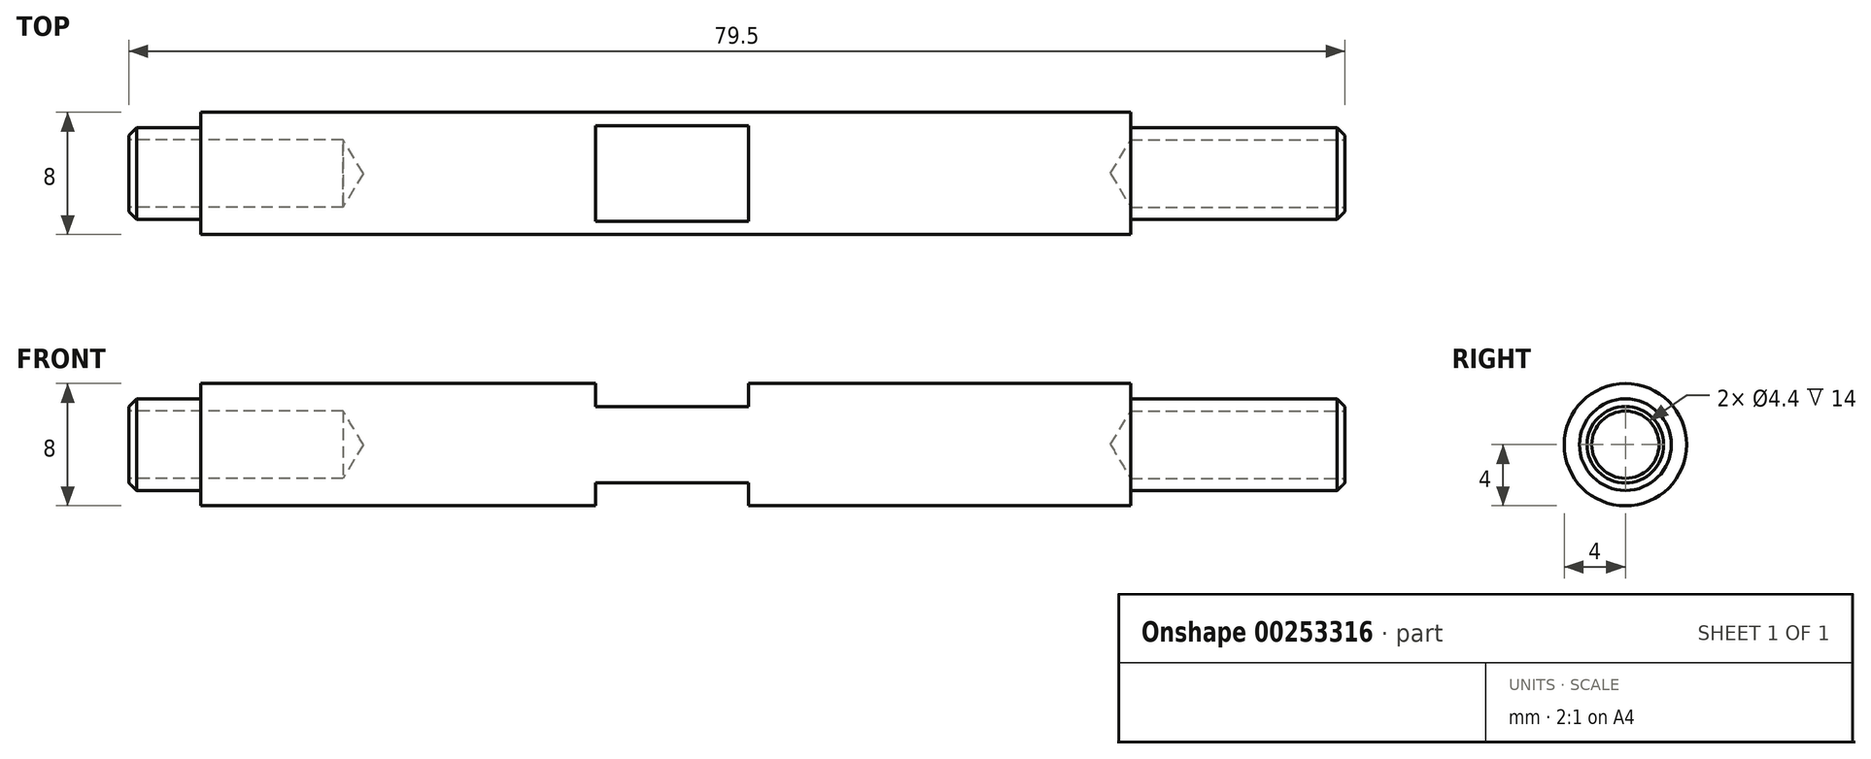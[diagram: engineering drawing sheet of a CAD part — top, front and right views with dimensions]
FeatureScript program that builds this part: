
annotation { "Feature Type Name" : "Feature", "Feature Type Description" : "" }
export const myFeature = defineFeature(function(context is Context, id is Id, definition is map)
    precondition{}
    {
        {
            var Q0;
            Q0=qCreatedBy(makeId("Top.planeOp"),FACE);
            var sketch = newSketch(context, id + "F0", { "sketchPlane" : qUnion([Q0])});
            skLineSegment(sketch, "E0.bottom", {"start": v(30.4, 4) * mm, "end": v(-30.4, 4) * mm});
            skLineSegment(sketch, "E0.top", {"start": v(30.4, -4) * mm, "end": v(-30.4, -4) * mm, "construction": true});
            skLineSegment(sketch, "E0.left", {"start": v(30.4, 4) * mm, "end": v(30.4, -4) * mm});
            skLineSegment(sketch, "E0.right", {"start": v(-30.4, 4) * mm, "end": v(-30.4, -4) * mm});
            skPoint(sketch, "E0.middle", {"position": v(0, 0) * mm});
            skLineSegment(sketch, "E1", {"start": v(30.4, 3) * mm, "end": v(44.4, 3) * mm});
            skLineSegment(sketch, "E2", {"start": v(44.4, 3) * mm, "end": v(44.4, -3) * mm});
            skLineSegment(sketch, "E3", {"start": v(44.4, -3) * mm, "end": v(30.4, -3) * mm, "construction": true});
            skLineSegment(sketch, "E4", {"start": v(-30.4, 3) * mm, "end": v(-35.1, 3) * mm});
            skLineSegment(sketch, "E5", {"start": v(-35.1, 3) * mm, "end": v(-35.1, -3) * mm});
            skLineSegment(sketch, "E6", {"start": v(-35.1, -3) * mm, "end": v(-30.4, -3) * mm, "construction": true});
            skLineSegment(sketch, "E7", {"start": v(-49.35, 0) * mm, "end": v(55.64, 0) * mm});
            skPoint(sketch, "E7.endSnap0", {"position": v(44.4, 0) * mm});
            skPoint(sketch, "E8", {"position": v(-35.1, 0) * mm});
            skSolve(sketch);
        }
        {
            var Q0;
            {var subQ0=sQuery(id+"F0.wireOp",EDGE,"E4");Q0=makeQuery(id+"F0.imprint","IMPRINT",FACE,{"disambiguationData":[TD([[makeQuery(id+"F0.imprint","IMPRINT",EDGE,{"derivedFrom":subQ0}),1.0]])]});}
            var Q1;
            {var subQ3=sQuery(id+"F0.wireOp",EDGE,"E0.bottom");Q1=makeQuery(id+"F0.imprint","IMPRINT",FACE,{"disambiguationData":[TD([[makeQuery(id+"F0.imprint","IMPRINT",EDGE,{"derivedFrom":subQ3}),1.0]])]});}
            var Q2;
            {var subQ0=sQuery(id+"F0.wireOp",EDGE,"E1");Q2=makeQuery(id+"F0.imprint","IMPRINT",FACE,{"disambiguationData":[TD([[makeQuery(id+"F0.imprint","IMPRINT",EDGE,{"derivedFrom":subQ0}),-1.0]])]});}
            var Q3;
            Q3=sQuery(id+"F0.wireOp",EDGE,"E7");
            revolve(context, id + "F1", {"entities" : qUnion([Q0, Q1, Q2]), "axis" : qUnion([Q3]), "revolveType" : RevolveType.FULL});
        }
        {
            var Q0;
            Q0=qCreatedBy(makeId("Front.planeOp"),FACE);
            var sketch = newSketch(context, id + "F2", { "sketchPlane" : qUnion([Q0])});
            skLineSegment(sketch, "E9.bottom", {"start": v(-4.6, 2.5) * mm, "end": v(5.4, 2.5) * mm});
            skLineSegment(sketch, "E9.top", {"start": v(-4.6, 6.68) * mm, "end": v(5.4, 6.68) * mm});
            skLineSegment(sketch, "E9.left", {"start": v(-4.6, 2.5) * mm, "end": v(-4.6, 6.68) * mm});
            skLineSegment(sketch, "E9.right", {"start": v(5.4, 2.5) * mm, "end": v(5.4, 6.68) * mm});
            skLineSegment(sketch, "E10.MirrorCS", {"start": v(-4.6, -2.5) * mm, "end": v(5.4, -2.5) * mm});
            skLineSegment(sketch, "E11.MirrorCS", {"start": v(-4.6, -2.5) * mm, "end": v(-4.6, -6.68) * mm});
            skLineSegment(sketch, "E12.MirrorCS", {"start": v(5.4, -2.5) * mm, "end": v(5.4, -6.68) * mm});
            skLineSegment(sketch, "E13.MirrorCS", {"start": v(-4.6, -6.68) * mm, "end": v(5.4, -6.68) * mm});
            skSolve(sketch);
        }
        {
            var Q0;
            Q0=makeQuery(id+"F2.imprint","IMPRINT",FACE,{"disambiguationData":[TD([[makeQuery(id+"F2.imprint","IMPRINT",EDGE,{"derivedFrom":sQuery(id+"F2.wireOp",EDGE,"E9.bottom")}),1.0]])]});
            var Q1;
            Q1=makeQuery(id+"F2.imprint","IMPRINT",FACE,{"disambiguationData":[TD([[makeQuery(id+"F2.imprint","IMPRINT",EDGE,{"derivedFrom":sQuery(id+"F2.wireOp",EDGE,"E10.MirrorCS")}),-1.0]])]});
            extrude(context, id + "F3", {"entities" : qUnion([Q0, Q1]), "operationType" : NewBodyOperationType.REMOVE, "endBound" : BoundingType.SYMMETRIC, "oppositeDirection" : true, "depth" : 25 * mm});
        }
        {
            var Q0;
            Q0=makeQuery(id+"F1.opRevolve","SWEPT_FACE",FACE,{"disambiguationData":[OSD([sQuery(id+"F0.wireOp",EDGE,"E2")])]});
            var sketch = newSketch(context, id + "F4", { "sketchPlane" : qUnion([Q0])});
            skPoint(sketch, "E14", {"position": v(0, 0) * mm});
            skSolve(sketch);
        }
        {
            var Q0;
            Q0=sQuery(id+"F4.wireOp",VERTEX,"E14");
            var Q1;
            Q1=makeQuery(id+"F1.opRevolve","SWEPT_BODY",BODY,{"disambiguationData":[OSD([sQuery(id+"F0.wireOp",EDGE,"E0.bottom"),sQuery(id+"F0.wireOp",EDGE,"E0.left"),sQuery(id+"F0.wireOp",EDGE,"E0.right"),sQuery(id+"F0.wireOp",EDGE,"E1"),sQuery(id+"F0.wireOp",EDGE,"E2"),sQuery(id+"F0.wireOp",EDGE,"E4"),sQuery(id+"F0.wireOp",EDGE,"E5"),sQuery(id+"F0.wireOp",EDGE,"E7")])]});
            hole(context, id + "F5", {"style" : HoleStyle.SIMPLE, "endStyle" : HoleEndStyle.BLIND, "standardTappedOrClearance" : lookupTablePath({ "standard" : "ISO", "fit" : "Normal", "size" : "M4", "type" : "Clearance" }), "standardBlindInLast" : lookupTablePath({ "fit" : "Standard", "standard" : "ISO", "size" : "M4", "type" : "Clearance" }), "holeDiameter" : 4.4 * mm, "holeDepth" : 14 * mm, "tappedDepth" : 12 * mm, "tapClearance" : 3, "locations" : qUnion([Q0]), "scope" : qUnion([Q1])});
        }
        {
            var Q0;
            Q0=makeQuery(id+"F1.opRevolve","SWEPT_FACE",FACE,{"disambiguationData":[OSD([sQuery(id+"F0.wireOp",EDGE,"E5")])]});
            var sketch = newSketch(context, id + "F6", { "sketchPlane" : qUnion([Q0])});
            skPoint(sketch, "E15", {"position": v(0, 0) * mm});
            skSolve(sketch);
        }
        {
            var Q0;
            Q0=sQuery(id+"F6.wireOp",VERTEX,"E15");
            var Q1;
            Q1=makeQuery(id+"F1.opRevolve","SWEPT_BODY",BODY,{"disambiguationData":[OSD([sQuery(id+"F0.wireOp",EDGE,"E0.bottom"),sQuery(id+"F0.wireOp",EDGE,"E0.left"),sQuery(id+"F0.wireOp",EDGE,"E0.right"),sQuery(id+"F0.wireOp",EDGE,"E1"),sQuery(id+"F0.wireOp",EDGE,"E2"),sQuery(id+"F0.wireOp",EDGE,"E4"),sQuery(id+"F0.wireOp",EDGE,"E5"),sQuery(id+"F0.wireOp",EDGE,"E7")])]});
            hole(context, id + "F7", {"style" : HoleStyle.SIMPLE, "endStyle" : HoleEndStyle.BLIND, "standardTappedOrClearance" : lookupTablePath({ "standard" : "ISO", "fit" : "Normal", "size" : "M4", "type" : "Clearance" }), "standardBlindInLast" : lookupTablePath({ "fit" : "Standard", "standard" : "ISO", "size" : "M4", "type" : "Clearance" }), "holeDiameter" : 4.4 * mm, "holeDepth" : 14 * mm, "tappedDepth" : 12 * mm, "tapClearance" : 3, "locations" : qUnion([Q0]), "scope" : qUnion([Q1])});
        }
        {
            var Q0;
            Q0=makeQuery(id+"F1.opRevolve","SWEPT_EDGE",EDGE,{"disambiguationData":[OSD([sQuery(id+"F0.wireOp",EDGE,"E4"),sQuery(id+"F0.wireOp",EDGE,"E5")])]});
            var Q1;
            Q1=makeQuery(id+"F1.opRevolve","SWEPT_EDGE",EDGE,{"disambiguationData":[OSD([sQuery(id+"F0.wireOp",EDGE,"E1"),sQuery(id+"F0.wireOp",EDGE,"E2")])]});
            chamfer(context, id + "F8", {"entities" : qUnion([Q0, Q1]), "width" : .5 * mm, "tangentPropagation" : true});
        }
    });
